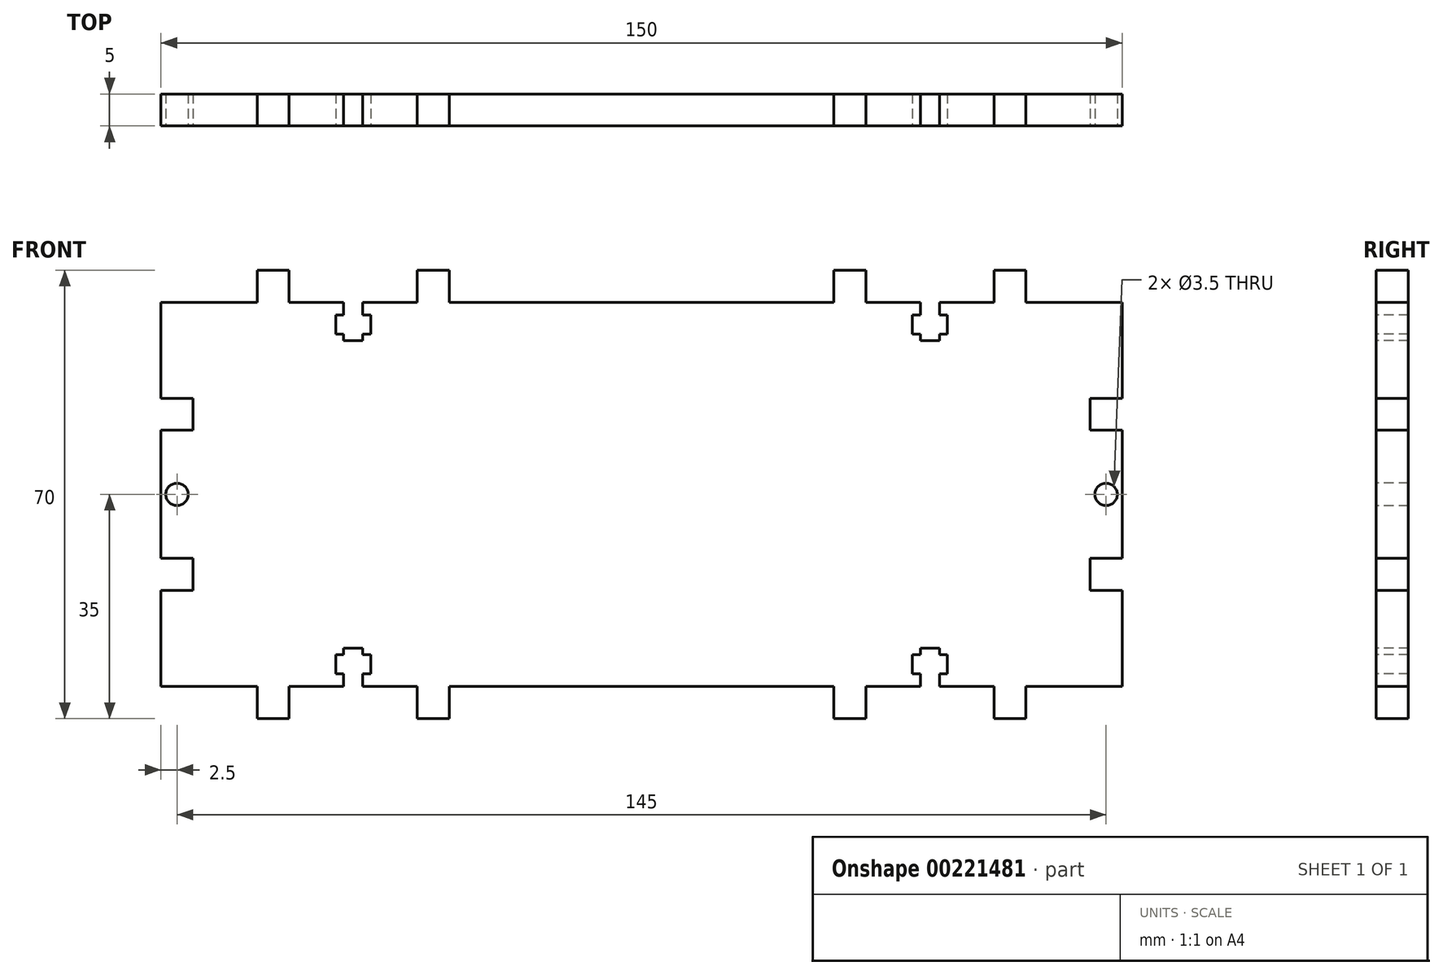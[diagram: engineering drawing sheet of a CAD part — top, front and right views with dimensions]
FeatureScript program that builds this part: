
annotation { "Feature Type Name" : "Feature", "Feature Type Description" : "" }
export const myFeature = defineFeature(function(context is Context, id is Id, definition is map)
    precondition{}
    {
        {
            var Q0;
            Q0=qCreatedBy(makeId("Top.planeOp"),FACE);
            var sketch = newSketch(context, id + "F0", { "sketchPlane" : qUnion([Q0])});
            skLineSegment(sketch, "E0.bottom", {"start": v(0, 0) * mm, "end": v(150, 0) * mm});
            skLineSegment(sketch, "E0.top", {"start": v(0, 5) * mm, "end": v(150, 5) * mm});
            skLineSegment(sketch, "E0.left", {"start": v(0, 0) * mm, "end": v(0, 5) * mm});
            skLineSegment(sketch, "E0.right", {"start": v(150, 0) * mm, "end": v(150, 5) * mm});
            skSolve(sketch);
        }
        {
            var Q0;
            Q0=makeQuery(id+"F0.imprint","IMPRINT",FACE,{"disambiguationData":[TD([[makeQuery(id+"F0.imprint","IMPRINT",EDGE,{"derivedFrom":sQuery(id+"F0.wireOp",EDGE,"E0.bottom")}),1.0]])]});
            extrude(context, id + "F1", {"entities" : qUnion([Q0]), "depth" : 60 * mm});
        }
        {
            var Q0;
            Q0=makeQuery(id+"F1.opExtrude","SWEPT_FACE",FACE,{"disambiguationData":[OSD([sQuery(id+"F0.wireOp",EDGE,"E0.bottom")])]});
            var sketch = newSketch(context, id + "F2", { "sketchPlane" : qUnion([Q0])});
            skLineSegment(sketch, "E1.bottom", {"start": v(15, 0) * mm, "end": v(20, 0) * mm});
            skLineSegment(sketch, "E1.top", {"start": v(15, -5) * mm, "end": v(20, -5) * mm});
            skLineSegment(sketch, "E1.left", {"start": v(15, 0) * mm, "end": v(15, -5) * mm});
            skLineSegment(sketch, "E1.right", {"start": v(20, 0) * mm, "end": v(20, -5) * mm});
            skLineSegment(sketch, "E2.bottom", {"start": v(40, 0) * mm, "end": v(45, 0) * mm});
            skLineSegment(sketch, "E2.top", {"start": v(40, -5) * mm, "end": v(45, -5) * mm});
            skLineSegment(sketch, "E2.left", {"start": v(40, 0) * mm, "end": v(40, -5) * mm});
            skLineSegment(sketch, "E2.right", {"start": v(45, 0) * mm, "end": v(45, -5) * mm});
            skLineSegment(sketch, "E3", {"start": v(75, 0) * mm, "end": v(75, 60) * mm, "construction": true});
            skLineSegment(sketch, "E4", {"start": v(0, 30) * mm, "end": v(150, 30) * mm, "construction": true});
            skLineSegment(sketch, "E5.MirrorCS", {"start": v(110, 0) * mm, "end": v(110, -5) * mm});
            skLineSegment(sketch, "E6.MirrorCS", {"start": v(105, 0) * mm, "end": v(105, -5) * mm});
            skLineSegment(sketch, "E7.MirrorCS", {"start": v(110, -5) * mm, "end": v(105, -5) * mm});
            skLineSegment(sketch, "E8.MirrorCS", {"start": v(110, 0) * mm, "end": v(105, 0) * mm});
            skLineSegment(sketch, "E9.MirrorCS", {"start": v(130, 0) * mm, "end": v(130, -5) * mm});
            skLineSegment(sketch, "E10.MirrorCS", {"start": v(135, 0) * mm, "end": v(135, -5) * mm});
            skLineSegment(sketch, "E11.MirrorCS", {"start": v(135, -5) * mm, "end": v(130, -5) * mm});
            skLineSegment(sketch, "E12.MirrorCS", {"start": v(135, 0) * mm, "end": v(130, 0) * mm});
            skLineSegment(sketch, "E13.MirrorCS", {"start": v(40, 60) * mm, "end": v(40, 65) * mm});
            skLineSegment(sketch, "E14.MirrorCS", {"start": v(40, 65) * mm, "end": v(45, 65) * mm});
            skLineSegment(sketch, "E15.MirrorCS", {"start": v(40, 60) * mm, "end": v(45, 60) * mm});
            skLineSegment(sketch, "E16.MirrorCS", {"start": v(20, 60) * mm, "end": v(20, 65) * mm});
            skLineSegment(sketch, "E17.MirrorCS", {"start": v(15, 60) * mm, "end": v(15, 65) * mm});
            skLineSegment(sketch, "E18.MirrorCS", {"start": v(15, 65) * mm, "end": v(20, 65) * mm});
            skLineSegment(sketch, "E19.MirrorCS", {"start": v(15, 60) * mm, "end": v(20, 60) * mm});
            skLineSegment(sketch, "E20.MirrorCS", {"start": v(135, 60) * mm, "end": v(135, 65) * mm});
            skLineSegment(sketch, "E21.MirrorCS", {"start": v(130, 60) * mm, "end": v(130, 65) * mm});
            skLineSegment(sketch, "E22.MirrorCS", {"start": v(110, 60) * mm, "end": v(105, 60) * mm});
            skLineSegment(sketch, "E23.MirrorCS", {"start": v(45, 60) * mm, "end": v(45, 65) * mm});
            skLineSegment(sketch, "E24.MirrorCS", {"start": v(135, 60) * mm, "end": v(130, 60) * mm});
            skLineSegment(sketch, "E25.MirrorCS", {"start": v(135, 65) * mm, "end": v(130, 65) * mm});
            skLineSegment(sketch, "E26.MirrorCS", {"start": v(110, 65) * mm, "end": v(105, 65) * mm});
            skLineSegment(sketch, "E27.MirrorCS", {"start": v(110, 60) * mm, "end": v(110, 65) * mm});
            skLineSegment(sketch, "E28.MirrorCS", {"start": v(105, 60) * mm, "end": v(105, 65) * mm});
            skSolve(sketch);
        }
        {
            var Q0;
            Q0 = qSketchRegion(id + "F2", true);
            var Q1;
            Q1=makeQuery(id+"F1.opExtrude","SWEPT_FACE",FACE,{"disambiguationData":[OSD([sQuery(id+"F0.wireOp",EDGE,"E0.top")])]});
            extrude(context, id + "F3", {"entities" : qUnion([Q0]), "operationType" : NewBodyOperationType.ADD, "endBound" : BoundingType.UP_TO_SURFACE, "oppositeDirection" : true, "endBoundEntityFace" : qUnion([Q1]), "depth" : 25 * mm});
        }
        {
            var Q0;
            Q0=makeQuery(id+"F3.boolean.opBoolean","MERGE",FACE,{"derivedFrom":[makeQuery(id+"F1.opExtrude","SWEPT_FACE",FACE,{"disambiguationData":[OSD([sQuery(id+"F0.wireOp",EDGE,"E0.bottom")])]}),makeQuery(id+"F3.opExtrude","CAP_FACE",FACE,{"disambiguationData":[OSD([sQuery(id+"F2.wireOp",EDGE,"E1.bottom"),sQuery(id+"F2.wireOp",EDGE,"E1.top"),sQuery(id+"F2.wireOp",EDGE,"E1.left"),sQuery(id+"F2.wireOp",EDGE,"E1.right")])],"isStart":true}),makeQuery(id+"F3.opExtrude","CAP_FACE",FACE,{"disambiguationData":[OSD([sQuery(id+"F2.wireOp",EDGE,"E2.bottom"),sQuery(id+"F2.wireOp",EDGE,"E2.top"),sQuery(id+"F2.wireOp",EDGE,"E2.left"),sQuery(id+"F2.wireOp",EDGE,"E2.right")])],"isStart":true}),makeQuery(id+"F3.opExtrude","CAP_FACE",FACE,{"disambiguationData":[OSD([sQuery(id+"F2.wireOp",EDGE,"E5.MirrorCS"),sQuery(id+"F2.wireOp",EDGE,"E6.MirrorCS"),sQuery(id+"F2.wireOp",EDGE,"E7.MirrorCS"),sQuery(id+"F2.wireOp",EDGE,"E8.MirrorCS")])],"isStart":true}),makeQuery(id+"F3.opExtrude","CAP_FACE",FACE,{"disambiguationData":[OSD([sQuery(id+"F2.wireOp",EDGE,"E9.MirrorCS"),sQuery(id+"F2.wireOp",EDGE,"E10.MirrorCS"),sQuery(id+"F2.wireOp",EDGE,"E11.MirrorCS"),sQuery(id+"F2.wireOp",EDGE,"E12.MirrorCS")])],"isStart":true}),makeQuery(id+"F3.opExtrude","CAP_FACE",FACE,{"disambiguationData":[OSD([sQuery(id+"F2.wireOp",EDGE,"E13.MirrorCS"),sQuery(id+"F2.wireOp",EDGE,"E14.MirrorCS"),sQuery(id+"F2.wireOp",EDGE,"E15.MirrorCS"),sQuery(id+"F2.wireOp",EDGE,"E23.MirrorCS")])],"isStart":true}),makeQuery(id+"F3.opExtrude","CAP_FACE",FACE,{"disambiguationData":[OSD([sQuery(id+"F2.wireOp",EDGE,"E16.MirrorCS"),sQuery(id+"F2.wireOp",EDGE,"E17.MirrorCS"),sQuery(id+"F2.wireOp",EDGE,"E18.MirrorCS"),sQuery(id+"F2.wireOp",EDGE,"E19.MirrorCS")])],"isStart":true}),makeQuery(id+"F3.opExtrude","CAP_FACE",FACE,{"disambiguationData":[OSD([sQuery(id+"F2.wireOp",EDGE,"E20.MirrorCS"),sQuery(id+"F2.wireOp",EDGE,"E21.MirrorCS"),sQuery(id+"F2.wireOp",EDGE,"E24.MirrorCS"),sQuery(id+"F2.wireOp",EDGE,"E25.MirrorCS")])],"isStart":true}),makeQuery(id+"F3.opExtrude","CAP_FACE",FACE,{"disambiguationData":[OSD([sQuery(id+"F2.wireOp",EDGE,"E22.MirrorCS"),sQuery(id+"F2.wireOp",EDGE,"E26.MirrorCS"),sQuery(id+"F2.wireOp",EDGE,"E27.MirrorCS"),sQuery(id+"F2.wireOp",EDGE,"E28.MirrorCS")])],"isStart":true}),makeQuery(id+"F3.opExtrude","CAP_FACE",FACE,{"disambiguationData":[OSD([sQuery(id+"F2.wireOp",EDGE,"a409461e-9a6c-40b4-bf51-24f98c17385d.bottom"),sQuery(id+"F2.wireOp",EDGE,"a409461e-9a6c-40b4-bf51-24f98c17385d.top"),sQuery(id+"F2.wireOp",EDGE,"a409461e-9a6c-40b4-bf51-24f98c17385d.left"),sQuery(id+"F2.wireOp",EDGE,"a409461e-9a6c-40b4-bf51-24f98c17385d.right")])],"isStart":true}),makeQuery(id+"F3.opExtrude","CAP_FACE",FACE,{"disambiguationData":[OSD([sQuery(id+"F2.wireOp",EDGE,"da60d496-b721-4d9c-8835-50d6b0d56d3c.bottom"),sQuery(id+"F2.wireOp",EDGE,"da60d496-b721-4d9c-8835-50d6b0d56d3c.top"),sQuery(id+"F2.wireOp",EDGE,"da60d496-b721-4d9c-8835-50d6b0d56d3c.left"),sQuery(id+"F2.wireOp",EDGE,"da60d496-b721-4d9c-8835-50d6b0d56d3c.right")])],"isStart":true}),makeQuery(id+"F3.opExtrude","CAP_FACE",FACE,{"disambiguationData":[OSD([sQuery(id+"F2.wireOp",EDGE,"2704353c-3130-41fa-bc24-460208ad23760.MirrorCS"),sQuery(id+"F2.wireOp",EDGE,"2704353c-3130-41fa-bc24-460208ad23764.MirrorCS"),sQuery(id+"F2.wireOp",EDGE,"2704353c-3130-41fa-bc24-460208ad23765.MirrorCS"),sQuery(id+"F2.wireOp",EDGE,"2704353c-3130-41fa-bc24-460208ad23766.MirrorCS")])],"isStart":true}),makeQuery(id+"F3.opExtrude","CAP_FACE",FACE,{"disambiguationData":[OSD([sQuery(id+"F2.wireOp",EDGE,"2704353c-3130-41fa-bc24-460208ad23761.MirrorCS"),sQuery(id+"F2.wireOp",EDGE,"2704353c-3130-41fa-bc24-460208ad23762.MirrorCS"),sQuery(id+"F2.wireOp",EDGE,"2704353c-3130-41fa-bc24-460208ad23763.MirrorCS"),sQuery(id+"F2.wireOp",EDGE,"2704353c-3130-41fa-bc24-460208ad23767.MirrorCS")])],"isStart":true})]});
            var sketch = newSketch(context, id + "F4", { "sketchPlane" : qUnion([Q0])});
            skLineSegment(sketch, "E29", {"start": v(75, 60) * mm, "end": v(75, 0) * mm, "construction": true});
            skLineSegment(sketch, "E30", {"start": v(0, 30) * mm, "end": v(150, 30) * mm, "construction": true});
            skLineSegment(sketch, "E31.bottom", {"start": v(28.5, 0) * mm, "end": v(31.5, 0) * mm});
            skLineSegment(sketch, "E31.top", {"start": v(28.5, 6) * mm, "end": v(31.5, 6) * mm});
            skLineSegment(sketch, "E31.left", {"start": v(28.5, 0) * mm, "end": v(28.5, 2) * mm});
            skLineSegment(sketch, "E31.right", {"start": v(31.5, 0) * mm, "end": v(31.5, 2) * mm});
            skPoint(sketch, "E32", {"position": v(30, 0) * mm});
            skLineSegment(sketch, "E33.bottom", {"start": v(27.25, 5) * mm, "end": v(28.5, 5) * mm});
            skLineSegment(sketch, "E33.top", {"start": v(27.25, 2) * mm, "end": v(28.5, 2) * mm});
            skLineSegment(sketch, "E33.left", {"start": v(27.25, 5) * mm, "end": v(27.25, 2) * mm});
            skLineSegment(sketch, "E33.right", {"start": v(32.75, 5) * mm, "end": v(32.75, 2) * mm});
            skLineSegment(sketch, "E34.trimOffspring", {"start": v(28.5, 5) * mm, "end": v(28.5, 6) * mm});
            skLineSegment(sketch, "E35.trimOffspring", {"start": v(31.5, 5) * mm, "end": v(31.5, 6) * mm});
            skLineSegment(sketch, "E36.trimOffspring", {"start": v(31.5, 5) * mm, "end": v(32.75, 5) * mm});
            skLineSegment(sketch, "E37.trimOffspring", {"start": v(31.5, 2) * mm, "end": v(32.75, 2) * mm});
            skPoint(sketch, "E38", {"position": v(30, 6) * mm});
            skLineSegment(sketch, "E39.MirrorCS", {"start": v(118.5, 5) * mm, "end": v(117.25, 5) * mm});
            skLineSegment(sketch, "E40.MirrorCS", {"start": v(121.5, 5) * mm, "end": v(121.5, 6) * mm});
            skLineSegment(sketch, "E41.MirrorCS", {"start": v(118.5, 5) * mm, "end": v(118.5, 6) * mm});
            skLineSegment(sketch, "E42.MirrorCS", {"start": v(122.75, 2) * mm, "end": v(121.5, 2) * mm});
            skLineSegment(sketch, "E43.MirrorCS", {"start": v(122.75, 5) * mm, "end": v(121.5, 5) * mm});
            skLineSegment(sketch, "E44.MirrorCS", {"start": v(118.5, 0) * mm, "end": v(118.5, 2) * mm});
            skLineSegment(sketch, "E45.MirrorCS", {"start": v(121.5, 0) * mm, "end": v(121.5, 2) * mm});
            skLineSegment(sketch, "E46.MirrorCS", {"start": v(118.5, 2) * mm, "end": v(117.25, 2) * mm});
            skLineSegment(sketch, "E47.MirrorCS", {"start": v(121.5, 6) * mm, "end": v(118.5, 6) * mm});
            skLineSegment(sketch, "E48.MirrorCS", {"start": v(121.5, 0) * mm, "end": v(118.5, 0) * mm});
            skPoint(sketch, "E49.MirrorP", {"position": v(120, 6) * mm});
            skLineSegment(sketch, "E50.MirrorCS", {"start": v(122.75, 5) * mm, "end": v(122.75, 2) * mm});
            skLineSegment(sketch, "E51.MirrorCS", {"start": v(117.25, 5) * mm, "end": v(117.25, 2) * mm});
            skPoint(sketch, "E52.MirrorP", {"position": v(120, 0) * mm});
            skLineSegment(sketch, "E53.MirrorCS", {"start": v(122.75, 55) * mm, "end": v(121.5, 55) * mm});
            skLineSegment(sketch, "E54.MirrorCS", {"start": v(31.5, 55) * mm, "end": v(32.75, 55) * mm});
            skLineSegment(sketch, "E55.MirrorCS", {"start": v(31.5, 55) * mm, "end": v(31.5, 54) * mm});
            skLineSegment(sketch, "E56.MirrorCS", {"start": v(28.5, 55) * mm, "end": v(28.5, 54) * mm});
            skLineSegment(sketch, "E57.MirrorCS", {"start": v(27.25, 58) * mm, "end": v(28.5, 58) * mm});
            skLineSegment(sketch, "E58.MirrorCS", {"start": v(27.25, 55) * mm, "end": v(28.5, 55) * mm});
            skLineSegment(sketch, "E59.MirrorCS", {"start": v(31.5, 60) * mm, "end": v(31.5, 58) * mm});
            skLineSegment(sketch, "E60.MirrorCS", {"start": v(28.5, 60) * mm, "end": v(28.5, 58) * mm});
            skLineSegment(sketch, "E61.MirrorCS", {"start": v(28.5, 54) * mm, "end": v(31.5, 54) * mm});
            skLineSegment(sketch, "E62.MirrorCS", {"start": v(28.5, 60) * mm, "end": v(31.5, 60) * mm});
            skLineSegment(sketch, "E63.MirrorCS", {"start": v(118.5, 60) * mm, "end": v(118.5, 58) * mm});
            skLineSegment(sketch, "E64.MirrorCS", {"start": v(118.5, 55) * mm, "end": v(118.5, 54) * mm});
            skLineSegment(sketch, "E65.MirrorCS", {"start": v(121.5, 60) * mm, "end": v(121.5, 58) * mm});
            skLineSegment(sketch, "E66.MirrorCS", {"start": v(31.5, 58) * mm, "end": v(32.75, 58) * mm});
            skLineSegment(sketch, "E67.MirrorCS", {"start": v(118.5, 58) * mm, "end": v(117.25, 58) * mm});
            skLineSegment(sketch, "E68.MirrorCS", {"start": v(122.75, 58) * mm, "end": v(121.5, 58) * mm});
            skLineSegment(sketch, "E69.MirrorCS", {"start": v(118.5, 55) * mm, "end": v(117.25, 55) * mm});
            skLineSegment(sketch, "E70.MirrorCS", {"start": v(121.5, 55) * mm, "end": v(121.5, 54) * mm});
            skLineSegment(sketch, "E71.MirrorCS", {"start": v(121.5, 54) * mm, "end": v(118.5, 54) * mm});
            skLineSegment(sketch, "E72.MirrorCS", {"start": v(121.5, 60) * mm, "end": v(118.5, 60) * mm});
            skLineSegment(sketch, "E73.MirrorCS", {"start": v(117.25, 55) * mm, "end": v(117.25, 58) * mm});
            skLineSegment(sketch, "E74.MirrorCS", {"start": v(32.75, 55) * mm, "end": v(32.75, 58) * mm});
            skLineSegment(sketch, "E75.MirrorCS", {"start": v(27.25, 55) * mm, "end": v(27.25, 58) * mm});
            skPoint(sketch, "E76.MirrorP", {"position": v(120, 54) * mm});
            skPoint(sketch, "E77.MirrorP", {"position": v(30, 60) * mm});
            skPoint(sketch, "E78.MirrorP", {"position": v(120, 60) * mm});
            skPoint(sketch, "E79.MirrorP", {"position": v(30, 54) * mm});
            skLineSegment(sketch, "E80.MirrorCS", {"start": v(122.75, 55) * mm, "end": v(122.75, 58) * mm});
            skPoint(sketch, "E81", {"position": v(0, 30) * mm});
            skPoint(sketch, "E82.MirrorP", {"position": v(150, 30) * mm});
            skCircle(sketch, "E83", {"center": v(2.5, 30) * mm, "radius": 1.75 * mm});
            skLineSegment(sketch, "E84.bottom", {"start": v(0, 45) * mm, "end": v(5, 45) * mm});
            skLineSegment(sketch, "E84.top", {"start": v(0, 40) * mm, "end": v(5, 40) * mm});
            skLineSegment(sketch, "E84.left", {"start": v(0, 45) * mm, "end": v(0, 40) * mm});
            skLineSegment(sketch, "E84.right", {"start": v(5, 45) * mm, "end": v(5, 40) * mm});
            skPoint(sketch, "E85", {"position": v(2.5, 40) * mm});
            skLineSegment(sketch, "E86.MirrorCS", {"start": v(0, 20) * mm, "end": v(5, 20) * mm});
            skLineSegment(sketch, "E87.MirrorCS", {"start": v(5, 15) * mm, "end": v(5, 20) * mm});
            skLineSegment(sketch, "E88.MirrorCS", {"start": v(0, 15) * mm, "end": v(5, 15) * mm});
            skLineSegment(sketch, "E89.MirrorCS", {"start": v(0, 15) * mm, "end": v(0, 20) * mm});
            skLineSegment(sketch, "E90.MirrorCS", {"start": v(145, 45) * mm, "end": v(145, 40) * mm});
            skLineSegment(sketch, "E91.MirrorCS", {"start": v(150, 45) * mm, "end": v(150, 40) * mm});
            skLineSegment(sketch, "E92.MirrorCS", {"start": v(150, 45) * mm, "end": v(145, 45) * mm});
            skLineSegment(sketch, "E93.MirrorCS", {"start": v(150, 40) * mm, "end": v(145, 40) * mm});
            skCircle(sketch, "E94.MirrorC", {"center": v(147.5, 30) * mm, "radius": 1.75 * mm});
            skLineSegment(sketch, "E95.MirrorCS", {"start": v(145, 15) * mm, "end": v(145, 20) * mm});
            skLineSegment(sketch, "E96.MirrorCS", {"start": v(150, 15) * mm, "end": v(145, 15) * mm});
            skLineSegment(sketch, "E97.MirrorCS", {"start": v(150, 20) * mm, "end": v(145, 20) * mm});
            skLineSegment(sketch, "E98.MirrorCS", {"start": v(150, 15) * mm, "end": v(150, 20) * mm});
            skSolve(sketch);
        }
        {
            var Q0;
            Q0 = qSketchRegion(id + "F4", true);
            var Q1;
            {var subQ0=sQuery(id+"F0.wireOp",EDGE,"E0.top");Q1=makeQuery(id+"F3.boolean.opBoolean","MERGE",FACE,{"derivedFrom":[makeQuery(id+"F1.opExtrude","SWEPT_FACE",FACE,{"disambiguationData":[OSD([subQ0])]}),makeQuery(id+"F3.opExtrude","CAP_FACE",FACE,{"disambiguationData":[OSD([subQ0]),ownerDisambiguation([makeQuery(id+"F3.opExtrude","SWEPT_BODY",BODY,{"disambiguationData":[OSD([sQuery(id+"F2.wireOp",EDGE,"E1.bottom"),sQuery(id+"F2.wireOp",EDGE,"E1.top"),sQuery(id+"F2.wireOp",EDGE,"E1.left"),sQuery(id+"F2.wireOp",EDGE,"E1.right")])]})])],"isStart":false}),makeQuery(id+"F3.opExtrude","CAP_FACE",FACE,{"disambiguationData":[OSD([subQ0]),ownerDisambiguation([makeQuery(id+"F3.opExtrude","SWEPT_BODY",BODY,{"disambiguationData":[OSD([sQuery(id+"F2.wireOp",EDGE,"E2.bottom"),sQuery(id+"F2.wireOp",EDGE,"E2.top"),sQuery(id+"F2.wireOp",EDGE,"E2.left"),sQuery(id+"F2.wireOp",EDGE,"E2.right")])]})])],"isStart":false}),makeQuery(id+"F3.opExtrude","CAP_FACE",FACE,{"disambiguationData":[OSD([subQ0]),ownerDisambiguation([makeQuery(id+"F3.opExtrude","SWEPT_BODY",BODY,{"disambiguationData":[OSD([sQuery(id+"F2.wireOp",EDGE,"E5.MirrorCS"),sQuery(id+"F2.wireOp",EDGE,"E6.MirrorCS"),sQuery(id+"F2.wireOp",EDGE,"E7.MirrorCS"),sQuery(id+"F2.wireOp",EDGE,"E8.MirrorCS")])]})])],"isStart":false}),makeQuery(id+"F3.opExtrude","CAP_FACE",FACE,{"disambiguationData":[OSD([subQ0]),ownerDisambiguation([makeQuery(id+"F3.opExtrude","SWEPT_BODY",BODY,{"disambiguationData":[OSD([sQuery(id+"F2.wireOp",EDGE,"E9.MirrorCS"),sQuery(id+"F2.wireOp",EDGE,"E10.MirrorCS"),sQuery(id+"F2.wireOp",EDGE,"E11.MirrorCS"),sQuery(id+"F2.wireOp",EDGE,"E12.MirrorCS")])]})])],"isStart":false}),makeQuery(id+"F3.opExtrude","CAP_FACE",FACE,{"disambiguationData":[OSD([subQ0]),ownerDisambiguation([makeQuery(id+"F3.opExtrude","SWEPT_BODY",BODY,{"disambiguationData":[OSD([sQuery(id+"F2.wireOp",EDGE,"E13.MirrorCS"),sQuery(id+"F2.wireOp",EDGE,"E14.MirrorCS"),sQuery(id+"F2.wireOp",EDGE,"E15.MirrorCS"),sQuery(id+"F2.wireOp",EDGE,"E23.MirrorCS")])]})])],"isStart":false}),makeQuery(id+"F3.opExtrude","CAP_FACE",FACE,{"disambiguationData":[OSD([subQ0]),ownerDisambiguation([makeQuery(id+"F3.opExtrude","SWEPT_BODY",BODY,{"disambiguationData":[OSD([sQuery(id+"F2.wireOp",EDGE,"E16.MirrorCS"),sQuery(id+"F2.wireOp",EDGE,"E17.MirrorCS"),sQuery(id+"F2.wireOp",EDGE,"E18.MirrorCS"),sQuery(id+"F2.wireOp",EDGE,"E19.MirrorCS")])]})])],"isStart":false}),makeQuery(id+"F3.opExtrude","CAP_FACE",FACE,{"disambiguationData":[OSD([subQ0]),ownerDisambiguation([makeQuery(id+"F3.opExtrude","SWEPT_BODY",BODY,{"disambiguationData":[OSD([sQuery(id+"F2.wireOp",EDGE,"E20.MirrorCS"),sQuery(id+"F2.wireOp",EDGE,"E21.MirrorCS"),sQuery(id+"F2.wireOp",EDGE,"E24.MirrorCS"),sQuery(id+"F2.wireOp",EDGE,"E25.MirrorCS")])]})])],"isStart":false}),makeQuery(id+"F3.opExtrude","CAP_FACE",FACE,{"disambiguationData":[OSD([subQ0]),ownerDisambiguation([makeQuery(id+"F3.opExtrude","SWEPT_BODY",BODY,{"disambiguationData":[OSD([sQuery(id+"F2.wireOp",EDGE,"E22.MirrorCS"),sQuery(id+"F2.wireOp",EDGE,"E26.MirrorCS"),sQuery(id+"F2.wireOp",EDGE,"E27.MirrorCS"),sQuery(id+"F2.wireOp",EDGE,"E28.MirrorCS")])]})])],"isStart":false}),makeQuery(id+"F3.opExtrude","CAP_FACE",FACE,{"disambiguationData":[OSD([subQ0]),ownerDisambiguation([makeQuery(id+"F3.opExtrude","SWEPT_BODY",BODY,{"disambiguationData":[OSD([sQuery(id+"F2.wireOp",EDGE,"a409461e-9a6c-40b4-bf51-24f98c17385d.bottom"),sQuery(id+"F2.wireOp",EDGE,"a409461e-9a6c-40b4-bf51-24f98c17385d.top"),sQuery(id+"F2.wireOp",EDGE,"a409461e-9a6c-40b4-bf51-24f98c17385d.left"),sQuery(id+"F2.wireOp",EDGE,"a409461e-9a6c-40b4-bf51-24f98c17385d.right")])]})])],"isStart":false}),makeQuery(id+"F3.opExtrude","CAP_FACE",FACE,{"disambiguationData":[OSD([subQ0]),ownerDisambiguation([makeQuery(id+"F3.opExtrude","SWEPT_BODY",BODY,{"disambiguationData":[OSD([sQuery(id+"F2.wireOp",EDGE,"da60d496-b721-4d9c-8835-50d6b0d56d3c.bottom"),sQuery(id+"F2.wireOp",EDGE,"da60d496-b721-4d9c-8835-50d6b0d56d3c.top"),sQuery(id+"F2.wireOp",EDGE,"da60d496-b721-4d9c-8835-50d6b0d56d3c.left"),sQuery(id+"F2.wireOp",EDGE,"da60d496-b721-4d9c-8835-50d6b0d56d3c.right")])]})])],"isStart":false}),makeQuery(id+"F3.opExtrude","CAP_FACE",FACE,{"disambiguationData":[OSD([subQ0]),ownerDisambiguation([makeQuery(id+"F3.opExtrude","SWEPT_BODY",BODY,{"disambiguationData":[OSD([sQuery(id+"F2.wireOp",EDGE,"2704353c-3130-41fa-bc24-460208ad23760.MirrorCS"),sQuery(id+"F2.wireOp",EDGE,"2704353c-3130-41fa-bc24-460208ad23764.MirrorCS"),sQuery(id+"F2.wireOp",EDGE,"2704353c-3130-41fa-bc24-460208ad23765.MirrorCS"),sQuery(id+"F2.wireOp",EDGE,"2704353c-3130-41fa-bc24-460208ad23766.MirrorCS")])]})])],"isStart":false}),makeQuery(id+"F3.opExtrude","CAP_FACE",FACE,{"disambiguationData":[OSD([subQ0]),ownerDisambiguation([makeQuery(id+"F3.opExtrude","SWEPT_BODY",BODY,{"disambiguationData":[OSD([sQuery(id+"F2.wireOp",EDGE,"2704353c-3130-41fa-bc24-460208ad23761.MirrorCS"),sQuery(id+"F2.wireOp",EDGE,"2704353c-3130-41fa-bc24-460208ad23762.MirrorCS"),sQuery(id+"F2.wireOp",EDGE,"2704353c-3130-41fa-bc24-460208ad23763.MirrorCS"),sQuery(id+"F2.wireOp",EDGE,"2704353c-3130-41fa-bc24-460208ad23767.MirrorCS")])]})])],"isStart":false})]});}
            extrude(context, id + "F5", {"entities" : qUnion([Q0]), "operationType" : NewBodyOperationType.REMOVE, "endBound" : BoundingType.UP_TO_SURFACE, "oppositeDirection" : true, "endBoundEntityFace" : qUnion([Q1]), "depth" : 25 * mm});
        }
    });
